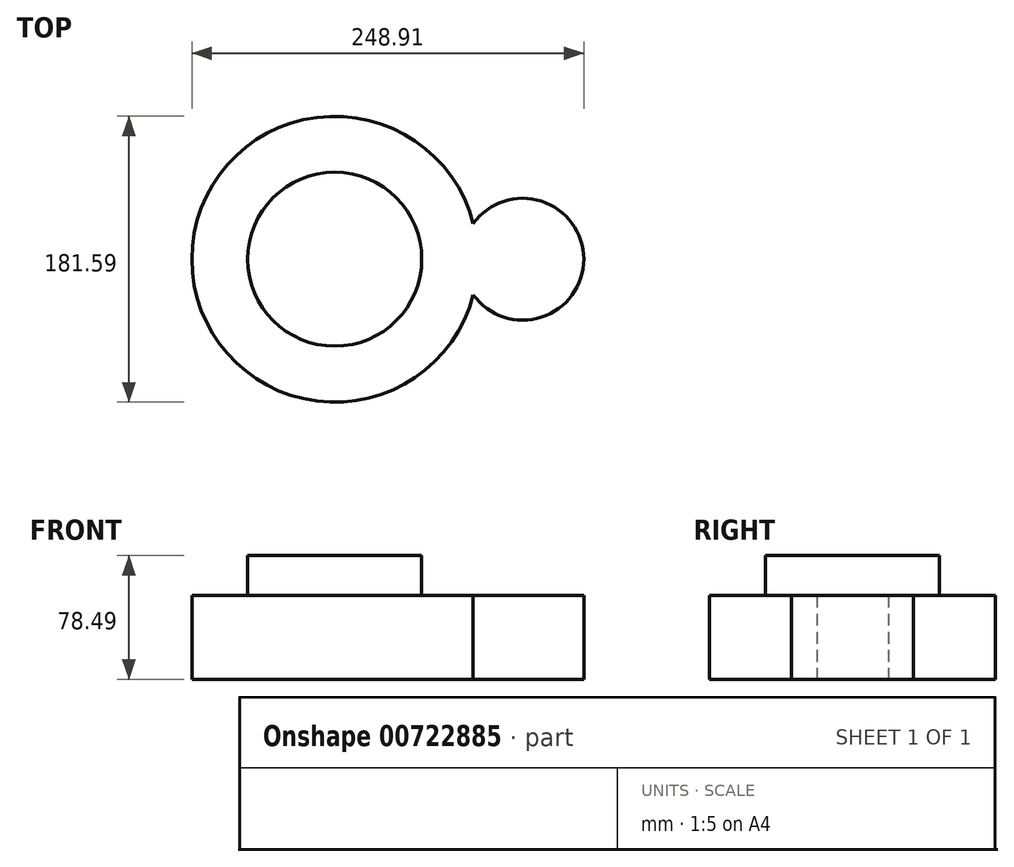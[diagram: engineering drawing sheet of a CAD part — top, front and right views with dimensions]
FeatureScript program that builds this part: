
annotation { "Feature Type Name" : "Feature", "Feature Type Description" : "" }
export const myFeature = defineFeature(function(context is Context, id is Id, definition is map)
    precondition{}
    {
        {
            var Q0;
            Q0=qCreatedBy(makeId("Top.planeOp"),FACE);
            var sketch = newSketch(context, id + "F0", { "sketchPlane" : qUnion([Q0])});
            skArc(sketch, "E0", {"start": v(0, 0) * mm, "mid": v(70.18, 22.59) * mm, "end": v(0, 45.17) * mm});
            skArc(sketch, "E1", {"start": v(0, 45.17) * mm, "mid": v(-178.73, 22.59) * mm, "end": v(0, 0) * mm});
            skSolve(sketch);
        }
        {
            var Q0;
            Q0=makeQuery(id+"F0.imprint","IMPRINT",FACE,{"disambiguationData":[TD([[makeQuery(id+"F0.imprint","IMPRINT",EDGE,{"derivedFrom":sQuery(id+"F0.wireOp",EDGE,"E0")}),1.0]])]});
            extrude(context, id + "F1", {"entities" : qUnion([Q0]), "depth" : 53.1 * mm, "offsetDistance" : 25.4 * mm});
        }
        {
            var Q0;
            Q0=makeQuery(id+"F1.opExtrude","CAP_FACE",FACE,{"disambiguationData":[OSD([sQuery(id+"F0.wireOp",EDGE,"E0"),sQuery(id+"F0.wireOp",EDGE,"E1")])],"isStart":false});
            var sketch = newSketch(context, id + "F2", { "sketchPlane" : qUnion([Q0])});
            skCircle(sketch, "E2", {"center": v(-87.94, 22.59) * mm, "radius": 55.23 * mm});
            skSolve(sketch);
        }
        {
            var Q0;
            Q0=makeQuery(id+"F2.imprint","IMPRINT",FACE,{"disambiguationData":[TD([[makeQuery(id+"F2.imprint","IMPRINT",EDGE,{"derivedFrom":sQuery(id+"F2.wireOp",EDGE,"E2")}),1.0]])]});
            extrude(context, id + "F3", {"entities" : qUnion([Q0]), "operationType" : NewBodyOperationType.ADD, "depth" : 25.4 * mm, "offsetDistance" : 25.4 * mm});
        }
    });
